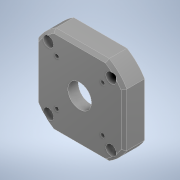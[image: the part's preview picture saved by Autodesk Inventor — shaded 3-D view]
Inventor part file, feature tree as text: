
AUTODESK INVENTOR PART (.ipt)
format: ipt  version: 2022 (Build 260153000, 153)  size: 184,320 bytes
history: mixed  units: in
note: dims shown in document units (in); Inventor stores cm internally (conversion verified against a paired STEP export)
features: extrude x3, sketch x3, chamfer x1, imported_body x1
ambient origin geometry x8: Origin, YZ Plane, XZ Plane, XY Plane, X Axis, Y Axis, Z Axis, Center Point
bodies: Solid1 (imported_parasolid)
feature tree (8):
  extrude  "Extrusion1"  Depth=0.3937in TaperAngle=0.0deg
  extrude  "Extrusion2"  Depth=0.3937in TaperAngle=0.0deg
  extrude  "Extrusion3"  TaperAngle=0.0deg  [1 undecoded]
  sketch  "Sketch1"  dims[d0=0.1102in d1=0.3937in d2=0.0in]
  sketch  "Sketch2"  dims[d3=0.5906in d4=0.3937in d5=0.0in]
  sketch  "Sketch3"  dims[d6=0.6299in d7=0.0in d8=0.0in]
  chamfer  "Chamfer2"  [1 undecoded]
  imported_body  NMx_Import_Brep_tag  [imported B-rep: ~32 faces, bbox_mm=[53.213203, 60.0, 14.0]]
note: 2 required parameter values undecoded (feature->parameter linkage not recoverable at this tier; creation-order binding heuristic only, values carry confidence <= 0.55)
